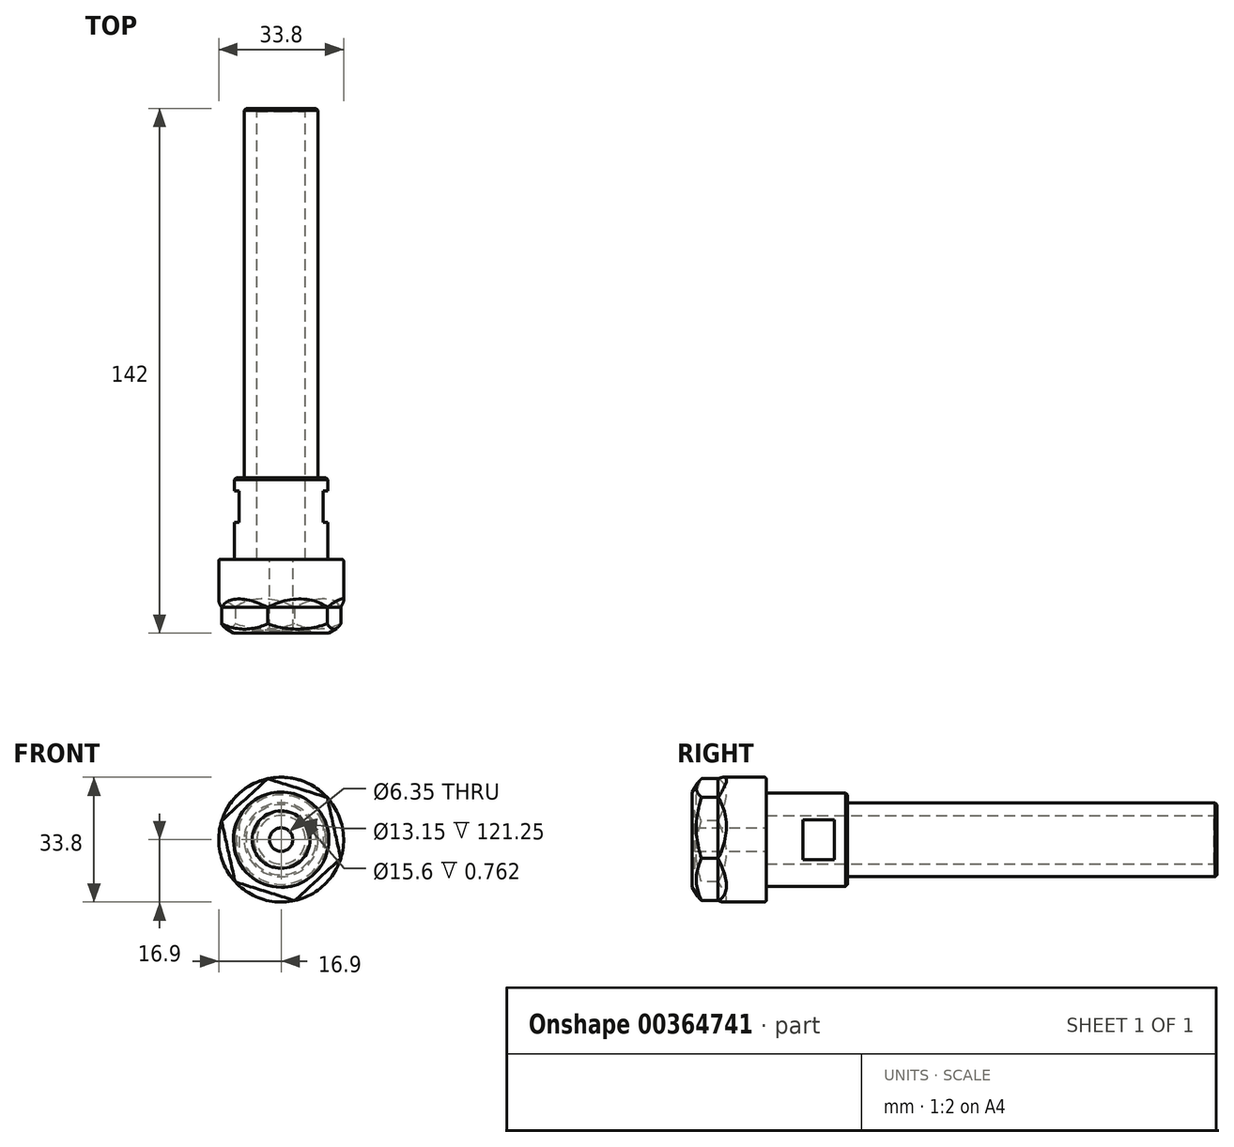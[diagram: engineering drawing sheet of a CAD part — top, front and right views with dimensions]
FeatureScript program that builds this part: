
annotation { "Feature Type Name" : "Feature", "Feature Type Description" : "" }
export const myFeature = defineFeature(function(context is Context, id is Id, definition is map)
    precondition{}
    {
        {
            var Q0;
            Q0=qCreatedBy(makeId("Front.planeOp"),FACE);
            var sketch = newSketch(context, id + "F0", { "sketchPlane" : qUnion([Q0])});
            skCircle(sketch, "E0", {"center": v(0, 0) * mm, "radius": 10 * mm});
            skCircle(sketch, "E1", {"center": v(0, 0) * mm, "radius": 6.58 * mm});
            skSolve(sketch);
        }
        {
            var Q0;
            Q0 = qSketchRegion(id + "F0", true);
            extrude(context, id + "F1", {"entities" : qUnion([Q0]), "depth" : 100 * mm});
        }
        {
            var Q0;
            Q0=makeQuery(id+"F1.opExtrude","CAP_FACE",FACE,{"disambiguationData":[OSD([sQuery(id+"F0.wireOp",EDGE,"E0"),sQuery(id+"F0.wireOp",EDGE,"E1")])],"isStart":false});
            var sketch = newSketch(context, id + "F2", { "sketchPlane" : qUnion([Q0])});
            skCircle(sketch, "E2", {"center": v(0, 0) * mm, "radius": 12.6 * mm});
            skCircle(sketch, "E3", {"center": v(0, 0) * mm, "radius": 6.58 * mm});
            skSolve(sketch);
        }
        {
            var Q0;
            Q0 = qSketchRegion(id + "F2", true);
            extrude(context, id + "F3", {"entities" : qUnion([Q0]), "operationType" : NewBodyOperationType.ADD, "depth" : 22 * mm});
        }
        {
            var Q0;
            Q0=makeQuery(id+"F3.opExtrude","CAP_FACE",FACE,{"disambiguationData":[OSD([sQuery(id+"F2.wireOp",EDGE,"E2"),sQuery(id+"F2.wireOp",EDGE,"E3")])],"isStart":false});
            var sketch = newSketch(context, id + "F4", { "sketchPlane" : qUnion([Q0])});
            skCircle(sketch, "E4.0", {"center": v(0, 0) * mm, "radius": 3.18 * mm});
            skCircle(sketch, "E5", {"center": v(0, 0) * mm, "radius": 16.9 * mm});
            skSolve(sketch);
        }
        {
            var Q0;
            Q0 = qSketchRegion(id + "F4", true);
            extrude(context, id + "F5", {"entities" : qUnion([Q0]), "operationType" : NewBodyOperationType.ADD, "depth" : 20 * mm});
        }
        {
            var Q0;
            Q0=makeQuery(id+"F5.opExtrude","CAP_FACE",FACE,{"disambiguationData":[OSD([sQuery(id+"F4.wireOp",EDGE,"E4.0"),sQuery(id+"F4.wireOp",EDGE,"E5")])],"isStart":false});
            var sketch = newSketch(context, id + "F6", { "sketchPlane" : qUnion([Q0])});
            skCircle(sketch, "E6", {"center": v(0, 0) * mm, "radius": 7.8 * mm});
            skSolve(sketch);
        }
        {
            var Q0;
            Q0 = qSketchRegion(id + "F6", true);
            extrude(context, id + "F7", {"entities" : qUnion([Q0]), "operationType" : NewBodyOperationType.REMOVE, "oppositeDirection" : true, "depth" : 0.76 * mm});
        }
        {
            var Q0;
            Q0=makeQuery(id+"F5.opExtrude","CAP_EDGE",EDGE,{"disambiguationData":[OSD([sQuery(id+"F4.wireOp",EDGE,"E5")])],"isStart":false});
            chamfer(context, id + "F8", {"entities" : qUnion([Q0]), "chamferType" : ChamferType.TWO_OFFSETS, "width1" : 4 * mm, "oppositeDirection" : false, "width2" : 2.5 * mm, "tangentPropagation" : true});
        }
        {
            var Q0;
            Q0=makeQuery(id+"F5.opExtrude","CAP_FACE",FACE,{"disambiguationData":[OSD([sQuery(id+"F4.wireOp",EDGE,"E4.0"),sQuery(id+"F4.wireOp",EDGE,"E5")])],"isStart":false});
            var sketch = newSketch(context, id + "F9", { "sketchPlane" : qUnion([Q0])});
            skCircle(sketch, "E7.cCircle", {"center": v(0, 0) * mm, "radius": 16.9 * mm, "construction": true});
            skLineSegment(sketch, "E7.0", {"start": v(12.45, 11.43) * mm, "end": v(16.12, -5.07) * mm});
            skLineSegment(sketch, "E7.1", {"start": v(16.12, -5.07) * mm, "end": v(3.67, -16.5) * mm});
            skLineSegment(sketch, "E7.2", {"start": v(3.67, -16.5) * mm, "end": v(-12.45, -11.43) * mm});
            skLineSegment(sketch, "E7.3", {"start": v(-12.45, -11.43) * mm, "end": v(-16.12, 5.07) * mm});
            skLineSegment(sketch, "E7.4", {"start": v(-16.12, 5.07) * mm, "end": v(-3.67, 16.5) * mm});
            skLineSegment(sketch, "E7.5", {"start": v(-3.67, 16.5) * mm, "end": v(12.45, 11.43) * mm});
            skCircle(sketch, "E8", {"center": v(0, 0) * mm, "radius": 21.1 * mm});
            skSolve(sketch);
        }
        {
            var Q0;
            {var subQ0=sQuery(id+"F9.wireOp",EDGE,"E7.0");Q0=makeQuery(id+"F9.imprint","IMPRINT",FACE,{"disambiguationData":[TD([[makeQuery(id+"F9.imprint","IMPRINT",EDGE,{"derivedFrom":subQ0}),1.0]])]});}
            var Q1;
            {var subQ0=sQuery(id+"F9.wireOp",EDGE,"E7.5");Q1=makeQuery(id+"F9.imprint","IMPRINT",FACE,{"disambiguationData":[TD([[makeQuery(id+"F9.imprint","IMPRINT",EDGE,{"derivedFrom":subQ0}),1.0]])]});}
            var Q2;
            {var subQ0=sQuery(id+"F9.wireOp",EDGE,"E7.4");Q2=makeQuery(id+"F9.imprint","IMPRINT",FACE,{"disambiguationData":[TD([[makeQuery(id+"F9.imprint","IMPRINT",EDGE,{"derivedFrom":subQ0}),1.0]])]});}
            var Q3;
            {var subQ0=sQuery(id+"F9.wireOp",EDGE,"E7.3");Q3=makeQuery(id+"F9.imprint","IMPRINT",FACE,{"disambiguationData":[TD([[makeQuery(id+"F9.imprint","IMPRINT",EDGE,{"derivedFrom":subQ0}),1.0]])]});}
            var Q4;
            {var subQ0=sQuery(id+"F9.wireOp",EDGE,"E7.2");Q4=makeQuery(id+"F9.imprint","IMPRINT",FACE,{"disambiguationData":[TD([[makeQuery(id+"F9.imprint","IMPRINT",EDGE,{"derivedFrom":subQ0}),1.0]])]});}
            var Q5;
            {var subQ0=sQuery(id+"F9.wireOp",EDGE,"E7.1");Q5=makeQuery(id+"F9.imprint","IMPRINT",FACE,{"disambiguationData":[TD([[makeQuery(id+"F9.imprint","IMPRINT",EDGE,{"derivedFrom":subQ0}),1.0]])]});}
            var Q6;
            Q6=makeQuery(id+"F9.imprint","IMPRINT",FACE,{"disambiguationData":[TD([[makeQuery(id+"F9.imprint","IMPRINT",EDGE,{"derivedFrom":sQuery(id+"F9.wireOp",EDGE,"E8")}),1.0]])]});
            extrude(context, id + "F10", {"entities" : qUnion([Q0, Q1, Q2, Q3, Q4, Q5, Q6]), "operationType" : NewBodyOperationType.REMOVE, "oppositeDirection" : true, "depth" : 10 * mm});
        }
        {
            var Q0;
            Q0=makeQuery(id+"F10.boolean.opBoolean","COPY",EDGE,{"derivedFrom":makeQuery(id+"F10.opExtrude","CAP_EDGE",EDGE,{"disambiguationData":[OSD([sQuery(id+"F9.wireOp",EDGE,"E7.5")])],"isStart":false})});
            chamfer(context, id + "F11", {"entities" : qUnion([Q0]), "width" : 3 * mm, "tangentPropagation" : true});
        }
        {
            var Q0;
            Q0=makeQuery(id+"F10.boolean.opBoolean","COPY",EDGE,{"derivedFrom":makeQuery(id+"F10.opExtrude","CAP_EDGE",EDGE,{"disambiguationData":[OSD([sQuery(id+"F9.wireOp",EDGE,"E7.4")])],"isStart":false})});
            chamfer(context, id + "F12", {"entities" : qUnion([Q0]), "width" : 3 * mm, "tangentPropagation" : true});
        }
        {
            var Q0;
            Q0=makeQuery(id+"F10.boolean.opBoolean","COPY",EDGE,{"derivedFrom":makeQuery(id+"F10.opExtrude","CAP_EDGE",EDGE,{"disambiguationData":[OSD([sQuery(id+"F9.wireOp",EDGE,"E7.3")])],"isStart":false})});
            chamfer(context, id + "F13", {"entities" : qUnion([Q0]), "width" : 3 * mm, "tangentPropagation" : true});
        }
        {
            var Q0;
            Q0=makeQuery(id+"F10.boolean.opBoolean","COPY",EDGE,{"derivedFrom":makeQuery(id+"F10.opExtrude","CAP_EDGE",EDGE,{"disambiguationData":[OSD([sQuery(id+"F9.wireOp",EDGE,"E7.2")])],"isStart":false})});
            chamfer(context, id + "F14", {"entities" : qUnion([Q0]), "width" : 3 * mm, "tangentPropagation" : true});
        }
        {
            var Q0;
            Q0=makeQuery(id+"F10.boolean.opBoolean","COPY",EDGE,{"derivedFrom":makeQuery(id+"F10.opExtrude","CAP_EDGE",EDGE,{"disambiguationData":[OSD([sQuery(id+"F9.wireOp",EDGE,"E7.1")])],"isStart":false})});
            chamfer(context, id + "F15", {"entities" : qUnion([Q0]), "width" : 3 * mm, "tangentPropagation" : true});
        }
        {
            var Q0;
            Q0=makeQuery(id+"F10.boolean.opBoolean","COPY",EDGE,{"derivedFrom":makeQuery(id+"F10.opExtrude","CAP_EDGE",EDGE,{"disambiguationData":[OSD([sQuery(id+"F9.wireOp",EDGE,"E7.0")])],"isStart":false})});
            chamfer(context, id + "F16", {"entities" : qUnion([Q0]), "width" : 3 * mm, "tangentPropagation" : true});
        }
        {
            var Q0;
            Q0=makeQuery(id+"F5.opExtrude","CAP_EDGE",EDGE,{"disambiguationData":[OSD([sQuery(id+"F4.wireOp",EDGE,"E5")])],"isStart":true});
            fillet(context, id + "F17", {"entities" : qUnion([Q0]), "radius" : .5 * mm, "tangentPropagation" : true, "allowEdgeOverflow" : false});
        }
        {
            var Q0;
            Q0=makeQuery(id+"F3.opExtrude","CAP_EDGE",EDGE,{"disambiguationData":[OSD([sQuery(id+"F2.wireOp",EDGE,"E2")])],"isStart":true});
            chamfer(context, id + "F18", {"entities" : qUnion([Q0]), "width" : .5 * mm, "tangentPropagation" : true});
        }
        {
            var Q0;
            Q0=qCreatedBy(makeId("Top.planeOp"),FACE);
            var sketch = newSketch(context, id + "F19", { "sketchPlane" : qUnion([Q0])});
            skLineSegment(sketch, "E9.bottom", {"start": v(11.37, -103.5) * mm, "end": v(15.01, -103.5) * mm});
            skLineSegment(sketch, "E9.top", {"start": v(11.37, -112) * mm, "end": v(15.01, -112) * mm});
            skLineSegment(sketch, "E9.left", {"start": v(11.37, -112) * mm, "end": v(11.37, -103.5) * mm});
            skLineSegment(sketch, "E9.right", {"start": v(15.01, -112) * mm, "end": v(15.01, -103.5) * mm});
            skLineSegment(sketch, "E10.bottom", {"start": v(-15.01, -103.5) * mm, "end": v(-11.37, -103.5) * mm});
            skLineSegment(sketch, "E10.top", {"start": v(-15.01, -112) * mm, "end": v(-11.37, -112) * mm});
            skLineSegment(sketch, "E10.left", {"start": v(-15.01, -112) * mm, "end": v(-15.01, -103.5) * mm});
            skLineSegment(sketch, "E10.right", {"start": v(-11.37, -112) * mm, "end": v(-11.37, -103.5) * mm});
            skLineSegment(sketch, "E11", {"start": v(0, -107.75) * mm, "end": v(11.37, -107.75) * mm, "construction": true});
            skLineSegment(sketch, "E12", {"start": v(0, -107.75) * mm, "end": v(-11.37, -107.75) * mm, "construction": true});
            skSolve(sketch);
        }
        {
            var Q0;
            Q0 = qSketchRegion(id + "F19", true);
            extrude(context, id + "F20", {"entities" : qUnion([Q0]), "operationType" : NewBodyOperationType.REMOVE, "endBound" : BoundingType.THROUGH_ALL, "depth" : 25.4 * mm, "hasSecondDirection" : true, "secondDirectionBound" : SecondDirectionBoundingType.THROUGH_ALL, "secondDirectionOppositeDirection" : true, "secondDirectionDepth" : 25.4 * mm});
        }
        {
            var Q0;
            Q0=makeQuery(id+"F1.opExtrude","CAP_EDGE",EDGE,{"disambiguationData":[OSD([sQuery(id+"F0.wireOp",EDGE,"E1")])],"isStart":true});
            chamfer(context, id + "F21", {"entities" : qUnion([Q0]), "width" : .75 * mm, "tangentPropagation" : true});
        }
        {
            var Q0;
            Q0=makeQuery(id+"F1.opExtrude","CAP_EDGE",EDGE,{"disambiguationData":[OSD([sQuery(id+"F0.wireOp",EDGE,"E0")])],"isStart":true});
            chamfer(context, id + "F22", {"entities" : qUnion([Q0]), "width" : .5 * mm, "tangentPropagation" : true});
        }
    });
